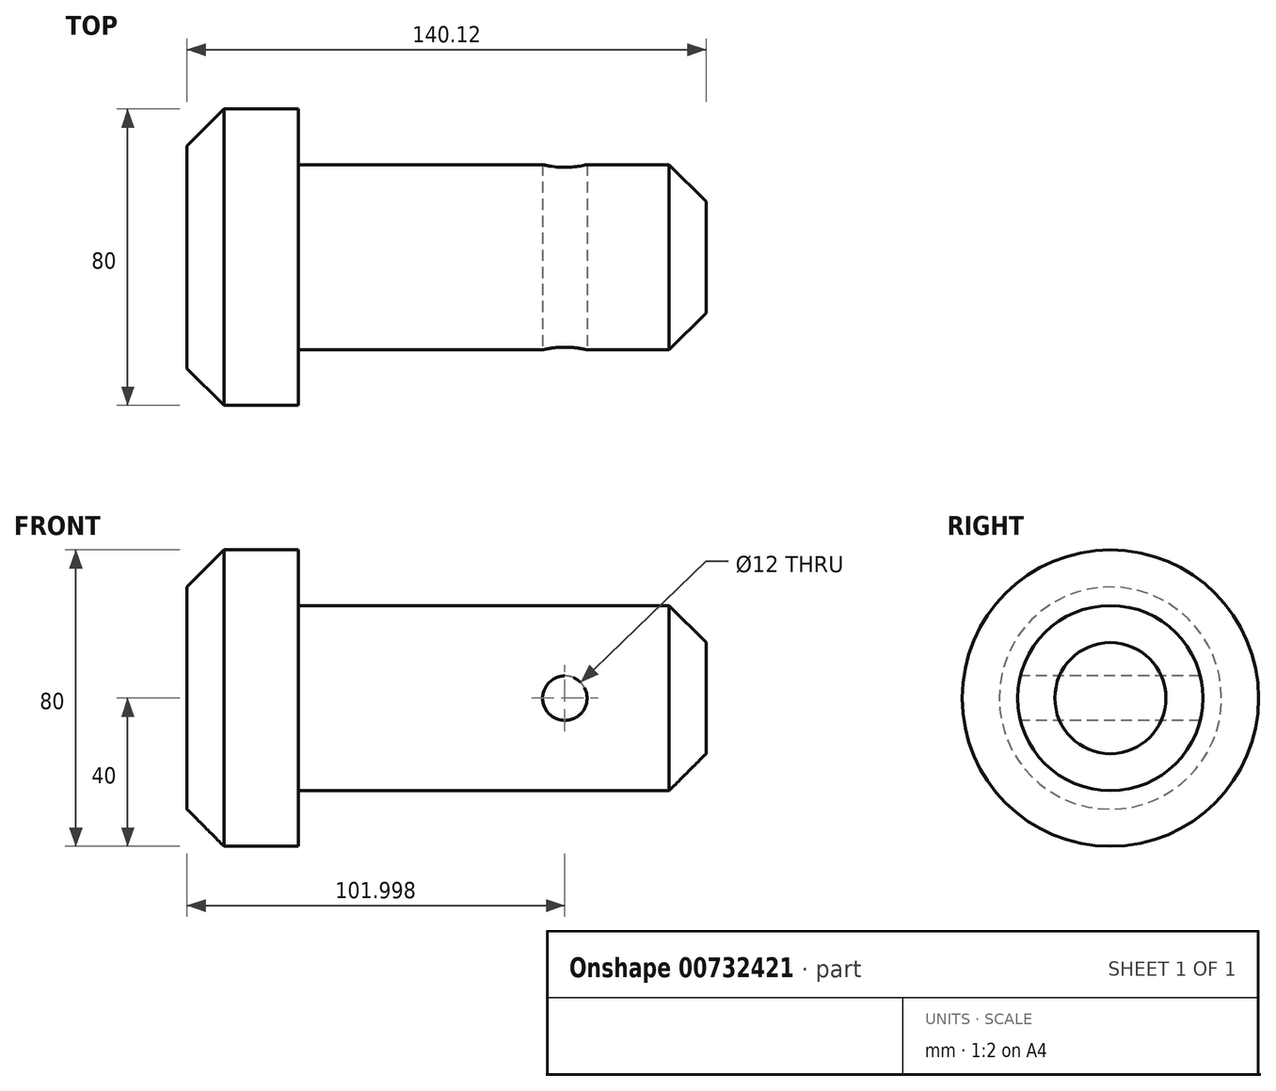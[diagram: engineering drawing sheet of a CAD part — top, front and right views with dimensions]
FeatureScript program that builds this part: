
annotation { "Feature Type Name" : "Feature", "Feature Type Description" : "" }
export const myFeature = defineFeature(function(context is Context, id is Id, definition is map)
    precondition{}
    {
        {
            var Q0;
            Q0=qCreatedBy(makeId("Front.planeOp"),FACE);
            var sketch = newSketch(context, id + "F0", { "sketchPlane" : qUnion([Q0])});
            skLineSegment(sketch, "E0", {"start": v(-406.36, 0) * mm, "end": v(-406.36, 30) * mm});
            skLineSegment(sketch, "E1", {"start": v(-406.36, 30) * mm, "end": v(-396.36, 40) * mm});
            skLineSegment(sketch, "E2", {"start": v(-396.36, 40) * mm, "end": v(-376.36, 40) * mm});
            skLineSegment(sketch, "E3", {"start": v(-376.36, 40) * mm, "end": v(-376.36, 25) * mm});
            skLineSegment(sketch, "E4", {"start": v(-376.36, 25) * mm, "end": v(-276.24, 25) * mm});
            skLineSegment(sketch, "E5", {"start": v(-276.24, 25) * mm, "end": v(-266.24, 15) * mm});
            skLineSegment(sketch, "E6", {"start": v(-266.24, 15) * mm, "end": v(-266.24, 0) * mm});
            skLineSegment(sketch, "E7", {"start": v(-266.24, 0) * mm, "end": v(-296.47, 0) * mm});
            skLineSegment(sketch, "E8.trimOffspring", {"start": v(-312.25, 0) * mm, "end": v(-406.36, 0) * mm});
            skLineSegment(sketch, "E9", {"start": v(-406.36, 0) * mm, "end": v(-266.24, 0) * mm});
            skSolve(sketch);
        }
        {
            var Q0;
            Q0=makeQuery(id+"F0.imprint","IMPRINT",FACE,{"disambiguationData":[TD([[makeQuery(id+"F0.imprint","IMPRINT",EDGE,{"derivedFrom":sQuery(id+"F0.wireOp",EDGE,"E0")}),-1.0]])]});
            var Q1;
            Q1=sQuery(id+"F0.wireOp",EDGE,"E7");
            revolve(context, id + "F1", {"surfaceOperationType" : NewSurfaceOperationType.NEW, "entities" : qUnion([Q0]), "axis" : qUnion([Q1]), "revolveType" : RevolveType.FULL});
        }
        {
            var Q0;
            Q0=qCreatedBy(makeId("Front.planeOp"),FACE);
            var sketch = newSketch(context, id + "F2", { "sketchPlane" : qUnion([Q0])});
            skCircle(sketch, "E10", {"center": v(-304.36, 0) * mm, "radius": 6 * mm});
            skSolve(sketch);
        }
        {
            var Q0;
            Q0 = qSketchRegion(id + "F2", true);
            extrude(context, id + "F3", {"entities" : qUnion([Q0]), "operationType" : NewBodyOperationType.REMOVE, "endBound" : BoundingType.THROUGH_ALL, "oppositeDirection" : true, "depth" : 25 * mm, "offsetDistance" : 25 * mm});
        }
        {
            var Q0;
            Q0=makeQuery(id+"F3.boolean.opBoolean","COPY",FACE,{"derivedFrom":makeQuery(id+"F3.opExtrude","CAP_FACE",FACE,{"disambiguationData":[OSD([sQuery(id+"F2.wireOp",EDGE,"E10")])],"isStart":true})});
            var sketch = newSketch(context, id + "F4", { "sketchPlane" : qUnion([Q0])});
            skSolve(sketch);
        }
        {
            var Q0;
            Q0=makeQuery(id+"F4.imprint","IMPRINT",FACE,{"disambiguationData":[TD([[makeQuery(id+"F4.imprint","IMPRINT",EDGE,{"derivedFrom":makeQuery(id+"F3.boolean.opBoolean","COPY",EDGE,{"derivedFrom":makeQuery(id+"F3.opExtrude","CAP_EDGE",EDGE,{"disambiguationData":[OSD([sQuery(id+"F2.wireOp",EDGE,"E10")])],"isStart":true})})}),-1.0]])]});
            extrude(context, id + "F5", {"entities" : qUnion([Q0]), "operationType" : NewBodyOperationType.REMOVE, "endBound" : BoundingType.THROUGH_ALL, "oppositeDirection" : true, "depth" : 13 * mm, "offsetDistance" : 25 * mm});
        }
        {
            var Q0;
            Q0 = qSketchRegion(id + "F2", true);
            extrude(context, id + "F6", {"entities" : qUnion([Q0]), "operationType" : NewBodyOperationType.REMOVE, "endBound" : BoundingType.THROUGH_ALL, "depth" : 25 * mm, "offsetDistance" : 25 * mm});
        }
    });
